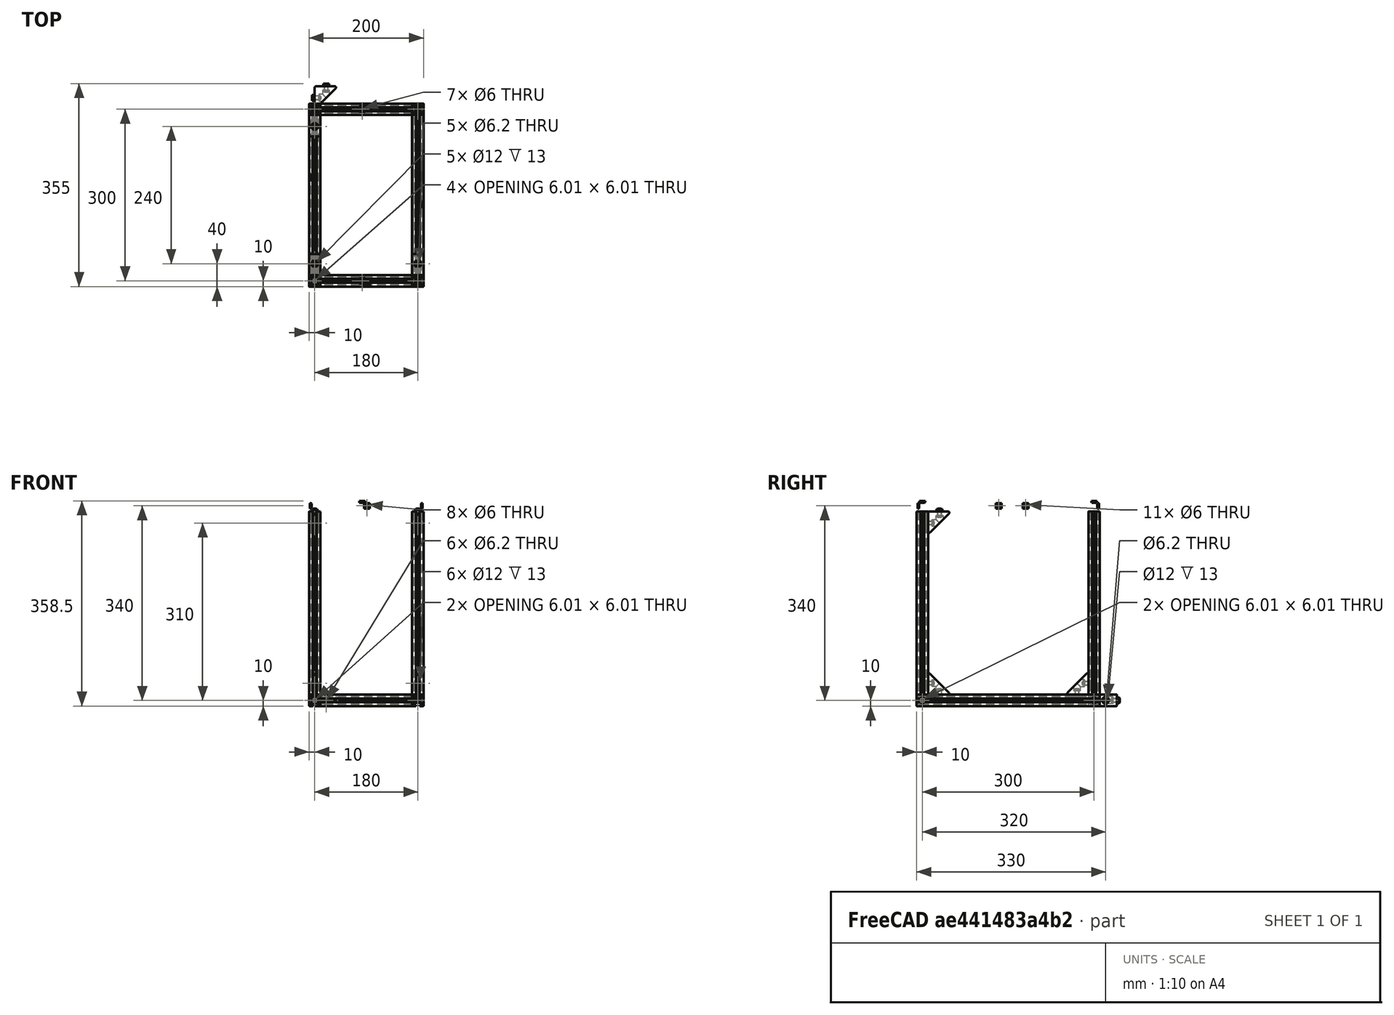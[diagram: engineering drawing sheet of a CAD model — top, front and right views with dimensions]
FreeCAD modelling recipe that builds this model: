
FCSTD DOCUMENT  (FreeCAD 0.17R9796 (Git))
Label: upperframe12
License: All rights reserved
LicenseURL: http://en.wikipedia.org/wiki/All_rights_reserved
objects: Part::Feature×55, Part::FeaturePython×16, App::Part×6, Part::Compound×5
note: 76 computed .brp shape members not serialized (recipe doc carries the construction recipe); baked Part::Feature solids carry a one-line shape summary decoded from their .brp

FEATURE [Part::Feature] Pocket003001  label="tslot32con"
  Placement = pos=(0,10,10) rot=(1,0,0;1.5708rad)
  shape: bbox 20 x 320 x 20 mm, 150 faces (baked)
FEATURE [Part::Feature] Pocket003002  label="tslot16"
  Placement = pos=(10,0,10) rot=(0,1,0;1.5708rad)
  shape: bbox 160 x 20 x 20 mm, 94 faces (baked)
FEATURE [Part::Feature] Pocket003006  label="tslot16_001"
  Placement = pos=(10,-300,10) rot=(0,1,0;1.5708rad)
  shape: bbox 160 x 20 x 20 mm, 94 faces (baked)
FEATURE [Part::Feature] Pocket003007  label="tslot32con_001"
  Placement = pos=(180,-310,10) rot=(0,0.707107,0.707107;3.14159rad)
  shape: bbox 20 x 320 x 20 mm, 150 faces (baked)
FEATURE [Part::FeaturePython] Screw  label="M6x25-Screw"  # Fasteners workbench fastener (typed FeaturePython)
  Placement = pos=(-4,0,10) rot=(0,-1,0;1.5708rad)
  diameter = 7
  invert = false
  length = 6
  matchOuter = false
  offset = 0
  thread = false
  type = 15
FEATURE [Part::FeaturePython] Screw001  label="M6x25-Screw004"  # Fasteners workbench fastener (typed FeaturePython)
  Placement = pos=(-4,-300,10) rot=(0,-1,0;1.5708rad)
  diameter = 7
  invert = false
  length = 6
  matchOuter = false
  offset = 0
  thread = false
  type = 15
FEATURE [Part::FeaturePython] Screw002  label="M6x25-Screw005"  # Fasteners workbench fastener (typed FeaturePython)
  Placement = pos=(184,0,10) rot=(0,1,0;1.5708rad)
  diameter = 7
  invert = false
  length = 6
  matchOuter = false
  offset = 0
  thread = false
  type = 15
FEATURE [Part::FeaturePython] Screw004  label="M6x25-Screw006"  # Fasteners workbench fastener (typed FeaturePython)
  Placement = pos=(184,-300,10) rot=(0,1,0;1.5708rad)
  diameter = 7
  invert = false
  length = 6
  matchOuter = false
  offset = 0
  thread = false
  type = 15
FEATURE [App::Part] Part  label="lower_frame"
  Group = -> [Pocket003001,Pocket003002,Pocket003006,Pocket003007,Screw,Screw001,Screw002,Screw004]
  License = CC BY 3.0
  LicenseURL = http://creativecommons.org/licenses/by/3.0/
  Origin = -> PartOrigin
FEATURE [Part::Feature] Pocket003008  label="tslot32con001"
  Placement = pos=(0,10,10) rot=(1,0,0;1.5708rad)
  shape: bbox 20 x 320 x 20 mm, 150 faces (baked)
FEATURE [Part::Feature] Pocket003009  label="tslot041"
  Placement = pos=(10,0,10) rot=(0,1,0;1.5708rad)
  shape: bbox 160 x 20 x 20 mm, 94 faces (baked)
FEATURE [Part::Feature] Pocket003010  label="tslot16_002"
  Placement = pos=(10,-300,10) rot=(0,1,0;1.5708rad)
  shape: bbox 160 x 20 x 20 mm, 94 faces (baked)
FEATURE [Part::Feature] Pocket003011  label="tslot32con_002"
  Placement = pos=(180,-310,10) rot=(0,0.707107,0.707107;3.14159rad)
  shape: bbox 20 x 320 x 20 mm, 150 faces (baked)
FEATURE [Part::FeaturePython] Screw005  label="M6x25-Screw012"  # Fasteners workbench fastener (typed FeaturePython)
  Placement = pos=(-4,0,10) rot=(0,-1,0;1.5708rad)
  diameter = 7
  invert = false
  length = 6
  matchOuter = false
  offset = 0
  thread = false
  type = 15
FEATURE [Part::FeaturePython] Screw006  label="M6x25-Screw015"  # Fasteners workbench fastener (typed FeaturePython)
  Placement = pos=(-4,-300,10) rot=(0,-1,0;1.5708rad)
  diameter = 7
  invert = false
  length = 6
  matchOuter = false
  offset = 0
  thread = false
  type = 15
FEATURE [Part::FeaturePython] Screw007  label="M6x25-Screw017"  # Fasteners workbench fastener (typed FeaturePython)
  Placement = pos=(184,0,10) rot=(0,1,0;1.5708rad)
  diameter = 7
  invert = false
  length = 6
  matchOuter = false
  offset = 0
  thread = false
  type = 15
FEATURE [Part::FeaturePython] Screw008  label="M6x25-Screw016"  # Fasteners workbench fastener (typed FeaturePython)
  Placement = pos=(184,-300,10) rot=(0,1,0;1.5708rad)
  diameter = 7
  invert = false
  length = 6
  matchOuter = false
  offset = 0
  thread = false
  type = 15
FEATURE [App::Part] Part001  label="upper_frame"
  Group = -> [Pocket003008,Pocket003009,Pocket003010,Pocket003011,Screw005,Screw006,Screw007,Screw008]
  License = CC BY 3.0
  LicenseURL = http://creativecommons.org/licenses/by/3.0/
  Origin = -> PartOrigin001
  Placement = pos=(0,0,340) rot=(0,0,1;0rad)
FEATURE [Part::Feature] Fillet004001  label="Fillet005"
  shape: bbox 37.5 x 37.5 x 20 mm, 26 faces (baked)
FEATURE [Part::FeaturePython] Screw009  label="M6x12-Screw"  # Fasteners workbench fastener (typed FeaturePython)
  Placement = pos=(7,20,10) rot=(0,1,0;1.5708rad)
  diameter = 4
  invert = false
  length = 1
  matchOuter = false
  offset = 0
  thread = false
  type = 20
FEATURE [Part::Feature] Body001  label="m6nutplate"
  Placement = pos=(-1.5,15,5) rot=(0,-1,0;1.5708rad)
  shape: bbox 3 x 10 x 10 mm, 9 faces (baked)
FEATURE [App::Part] Part002  label="cornerstonescrewnut"
  License = CC BY 3.0
  LicenseURL = http://creativecommons.org/licenses/by/3.0/
  Origin = -> PartOrigin002
  Placement = pos=(10,-50,20) rot=(0,-1,0;1.5708rad)
FEATURE [Part::FeaturePython] Screw010  label="M6x12-Screw001"  # Fasteners workbench fastener (typed FeaturePython)
  Placement = pos=(20,33,10) rot=(1,0,0;1.5708rad)
  diameter = 4
  invert = false
  length = 1
  matchOuter = false
  offset = 0
  thread = false
  type = 20
FEATURE [Part::Feature] Body002  label="m6nutplate001"
  Placement = pos=(15,41.5,5) rot=(0.57735,0.57735,0.57735;4.18879rad)
  shape: bbox 10 x 3 x 10 mm, 9 faces (baked)
FEATURE [Part::Feature] Fillet004002  label="Fillet006"
  shape: bbox 37.5 x 37.5 x 20 mm, 26 faces (baked)
FEATURE [Part::FeaturePython] Screw011  label="M6x12-Screw002"  # Fasteners workbench fastener (typed FeaturePython)
  Placement = pos=(7,20,10) rot=(0,1,0;1.5708rad)
  diameter = 4
  invert = false
  length = 1
  matchOuter = false
  offset = 0
  thread = false
  type = 20
FEATURE [Part::Feature] Body003  label="m6nutplate002"
  Placement = pos=(-1.5,15,5) rot=(0,-1,0;1.5708rad)
  shape: bbox 3 x 10 x 10 mm, 9 faces (baked)
FEATURE [Part::FeaturePython] Screw012  label="M6x12-Screw003"  # Fasteners workbench fastener (typed FeaturePython)
  Placement = pos=(20,33,10) rot=(1,0,0;1.5708rad)
  diameter = 4
  invert = false
  length = 1
  matchOuter = false
  offset = 0
  thread = false
  type = 20
FEATURE [Part::Feature] Body004  label="m6nutplate003"
  Placement = pos=(15,41.5,5) rot=(0.57735,0.57735,0.57735;4.18879rad)
  shape: bbox 10 x 3 x 10 mm, 9 faces (baked)
FEATURE [App::Part] Part003  label="cornerstonescrewnut001"
  Group = -> [Body003,Screw011,Fillet004002,Screw012,Body004,PartOrigin002,Body001,Screw009,Fillet004001,Screw010,Body002,Part002]
  License = CC BY 3.0
  LicenseURL = http://creativecommons.org/licenses/by/3.0/
  Origin = -> PartOrigin003
  Placement = pos=(190,-50,20) rot=(0,-1,0;1.5708rad)
FEATURE [Part::Feature] Fillet004003  label="Fillet007"
  shape: bbox 37.5 x 37.5 x 20 mm, 26 faces (baked)
FEATURE [Part::FeaturePython] Screw013  label="M6x12-Screw004"  # Fasteners workbench fastener (typed FeaturePython)
  Placement = pos=(7,20,10) rot=(0,1,0;1.5708rad)
  diameter = 4
  invert = false
  length = 1
  matchOuter = false
  offset = 0
  thread = false
  type = 20
FEATURE [Part::Feature] Body005  label="m6nutplate004"
  Placement = pos=(-1.5,15,5) rot=(0,-1,0;1.5708rad)
  shape: bbox 3 x 10 x 10 mm, 9 faces (baked)
FEATURE [Part::FeaturePython] Screw014  label="M6x12-Screw005"  # Fasteners workbench fastener (typed FeaturePython)
  Placement = pos=(20,33,10) rot=(1,0,0;1.5708rad)
  diameter = 4
  invert = false
  length = 1
  matchOuter = false
  offset = 0
  thread = false
  type = 20
FEATURE [Part::Feature] Body006  label="m6nutplate005"
  Placement = pos=(15,41.5,5) rot=(0.57735,0.57735,0.57735;4.18879rad)
  shape: bbox 10 x 3 x 10 mm, 9 faces (baked)
FEATURE [App::Part] Part004  label="cornerstonescrewnut002"
  Group = -> [Body005,Screw013,Fillet004003,Screw014,Body006]
  License = CC BY 3.0
  LicenseURL = http://creativecommons.org/licenses/by/3.0/
  Origin = -> PartOrigin004
  Placement = pos=(-10,-50,340) rot=(0,1,0;1.5708rad)
FEATURE [Part::Feature] Fillet004004  label="Fillet008"
  shape: bbox 37.5 x 37.5 x 20 mm, 26 faces (baked)
FEATURE [Part::FeaturePython] Screw015  label="M6x12-Screw006"  # Fasteners workbench fastener (typed FeaturePython)
  Placement = pos=(7,20,10) rot=(0,1,0;1.5708rad)
  diameter = 4
  invert = false
  length = 1
  matchOuter = false
  offset = 0
  thread = false
  type = 20
FEATURE [Part::Feature] Body007  label="m6nutplate006"
  Placement = pos=(-1.5,15,5) rot=(0,-1,0;1.5708rad)
  shape: bbox 3 x 10 x 10 mm, 9 faces (baked)
FEATURE [Part::FeaturePython] Screw016  label="M6x12-Screw007"  # Fasteners workbench fastener (typed FeaturePython)
  Placement = pos=(20,33,10) rot=(1,0,0;1.5708rad)
  diameter = 4
  invert = false
  length = 1
  matchOuter = false
  offset = 0
  thread = false
  type = 20
FEATURE [Part::Feature] Body008  label="m6nutplate007"
  Placement = pos=(15,41.5,5) rot=(0.57735,0.57735,0.57735;4.18879rad)
  shape: bbox 10 x 3 x 10 mm, 9 faces (baked)
FEATURE [App::Part] Part005  label="cornerstonescrewnut003"
  Group = -> [Body007,Screw015,Fillet004004,Screw016,Body008]
  License = CC BY 3.0
  LicenseURL = http://creativecommons.org/licenses/by/3.0/
  Origin = -> PartOrigin005
  Placement = pos=(170,-50,340) rot=(0,1,0;1.5708rad)
FEATURE [Part::Feature] Body009001  label="m6nutplate010"
  Placement = pos=(-1.5,15,5) rot=(0,-1,0;1.5708rad)
  shape: bbox 3 x 10 x 10 mm, 9 faces (baked)
FEATURE [Part::Feature] Body010001  label="m6nutplate011"
  Placement = pos=(15,41.5,5) rot=(0.57735,0.57735,0.57735;4.18879rad)
  shape: bbox 10 x 3 x 10 mm, 9 faces (baked)
FEATURE [Part::Feature] Screw018001  label="M6x12-Screw010"
  Placement = pos=(20,33,10) rot=(1,0,0;1.5708rad)
  shape: bbox 10.5 x 15.3 x 10.5 mm, 15 faces (baked)
FEATURE [Part::Feature] Screw017001  label="M6x12-Screw011"
  Placement = pos=(7,20,10) rot=(0,1,0;1.5708rad)
  shape: bbox 15.3 x 10.5 x 10.5 mm, 15 faces (baked)
FEATURE [Part::Feature] Fillet004005001  label="Fillet010"
  shape: bbox 37.5 x 37.5 x 20 mm, 26 faces (baked)
FEATURE [Part::Compound] Compound
  Links = -> [Body009001,Fillet004005001,Screw017001,Body010001,Screw018001]
  Placement = pos=(10,-250,340) rot=(0.707107,0,-0.707107;3.14159rad)
FEATURE [Part::Feature] Body010002  label="m6nutplate012"
  Placement = pos=(-1.5,15,5) rot=(0,-1,0;1.5708rad)
  shape: bbox 3 x 10 x 10 mm, 9 faces (baked)
FEATURE [Part::Feature] Body010003  label="m6nutplate013"
  Placement = pos=(15,41.5,5) rot=(0.57735,0.57735,0.57735;4.18879rad)
  shape: bbox 10 x 3 x 10 mm, 9 faces (baked)
FEATURE [Part::Feature] Screw018002  label="M6x12-Screw012"
  Placement = pos=(20,33,10) rot=(1,0,0;1.5708rad)
  shape: bbox 10.5 x 15.3 x 10.5 mm, 15 faces (baked)
FEATURE [Part::Feature] Screw018003  label="M6x12-Screw013"
  Placement = pos=(7,20,10) rot=(0,1,0;1.5708rad)
  shape: bbox 15.3 x 10.5 x 10.5 mm, 15 faces (baked)
FEATURE [Part::Feature] Fillet004005002  label="Fillet011"
  shape: bbox 37.5 x 37.5 x 20 mm, 26 faces (baked)
FEATURE [Part::Compound] Compound001
  Links = -> [Body010002,Fillet004005002,Screw018003,Body010003,Screw018002]
  Placement = pos=(190,-250,340) rot=(0.707107,0,-0.707107;3.14159rad)
FEATURE [Part::Feature] Body010004  label="m6nutplate014"
  Placement = pos=(-1.5,15,5) rot=(0,-1,0;1.5708rad)
  shape: bbox 3 x 10 x 10 mm, 9 faces (baked)
FEATURE [Part::Feature] Body010005  label="m6nutplate015"
  Placement = pos=(15,41.5,5) rot=(0.57735,0.57735,0.57735;4.18879rad)
  shape: bbox 10 x 3 x 10 mm, 9 faces (baked)
FEATURE [Part::Feature] Screw018004  label="M6x12-Screw014"
  Placement = pos=(20,33,10) rot=(1,0,0;1.5708rad)
  shape: bbox 10.5 x 15.3 x 10.5 mm, 15 faces (baked)
FEATURE [Part::Feature] Screw018005  label="M6x12-Screw015"
  Placement = pos=(7,20,10) rot=(0,1,0;1.5708rad)
  shape: bbox 15.3 x 10.5 x 10.5 mm, 15 faces (baked)
FEATURE [Part::Feature] Fillet004005003  label="Fillet012"
  shape: bbox 37.5 x 37.5 x 20 mm, 26 faces (baked)
FEATURE [Part::Compound] Compound002
  Links = -> [Body010004,Fillet004005003,Screw018005,Body010005,Screw018004]
  Placement = pos=(10,-290,60) rot=(0.57735,0.57735,-0.57735;4.18879rad)
FEATURE [Part::Feature] Body010006  label="m6nutplate016"
  Placement = pos=(-1.5,15,5) rot=(0,-1,0;1.5708rad)
  shape: bbox 3 x 10 x 10 mm, 9 faces (baked)
FEATURE [Part::Feature] Body010007  label="m6nutplate017"
  Placement = pos=(15,41.5,5) rot=(0.57735,0.57735,0.57735;4.18879rad)
  shape: bbox 10 x 3 x 10 mm, 9 faces (baked)
FEATURE [Part::Feature] Screw018006  label="M6x12-Screw016"
  Placement = pos=(20,33,10) rot=(1,0,0;1.5708rad)
  shape: bbox 10.5 x 15.3 x 10.5 mm, 15 faces (baked)
FEATURE [Part::Feature] Screw018007  label="M6x12-Screw017"
  Placement = pos=(7,20,10) rot=(0,1,0;1.5708rad)
  shape: bbox 15.3 x 10.5 x 10.5 mm, 15 faces (baked)
FEATURE [Part::Feature] Fillet004005004  label="Fillet013"
  shape: bbox 37.5 x 37.5 x 20 mm, 26 faces (baked)
FEATURE [Part::Compound] Compound003
  Links = -> [Body010006,Fillet004005004,Screw018007,Body010007,Screw018006]
  Placement = pos=(190,-290,60) rot=(0.57735,0.57735,-0.57735;4.18879rad)
FEATURE [Part::Feature] Pocket001001  label="tslot32"
  Placement = pos=(0,0,20) rot=(0,0,1;0rad)
  shape: bbox 20 x 20 x 320 mm, 94 faces (baked)
FEATURE [Part::Feature] Body010008  label="m6nutplate018"
  Placement = pos=(-1.5,15,5) rot=(0,-1,0;1.5708rad)
  shape: bbox 3 x 10 x 10 mm, 9 faces (baked)
FEATURE [Part::Feature] Body010009  label="m6nutplate019"
  Placement = pos=(15,41.5,5) rot=(0.57735,0.57735,0.57735;4.18879rad)
  shape: bbox 10 x 3 x 10 mm, 9 faces (baked)
FEATURE [Part::Feature] Screw018008  label="M6x12-Screw018"
  Placement = pos=(20,33,10) rot=(1,0,0;1.5708rad)
  shape: bbox 10.5 x 15.3 x 10.5 mm, 15 faces (baked)
FEATURE [Part::Feature] Screw018009  label="M6x12-Screw019"
  Placement = pos=(7,20,10) rot=(0,1,0;1.5708rad)
  shape: bbox 15.3 x 10.5 x 10.5 mm, 15 faces (baked)
FEATURE [Part::Feature] Fillet004005005  label="Fillet014"
  shape: bbox 37.5 x 37.5 x 20 mm, 26 faces (baked)
FEATURE [Part::Compound] Compound004
  Links = -> [Body010008,Fillet004005005,Screw018009,Body010009,Screw018008]
  Placement = pos=(-10,-10,60) rot=(0.57735,-0.57735,0.57735;4.18879rad)
FEATURE [Part::Feature] Pocket003012  label="tslot32_001"
  Placement = pos=(0,-300,20) rot=(0,0,1;0rad)
  shape: bbox 20 x 20 x 320 mm, 94 faces (baked)
FEATURE [Part::Feature] Pocket003013  label="tslot32_002"
  Placement = pos=(180,0,20) rot=(0,0,1;0rad)
  shape: bbox 20 x 20 x 320 mm, 94 faces (baked)
FEATURE [Part::Feature] Pocket003014  label="tslot32_003"
  Placement = pos=(180,-300,20) rot=(0,0,1;0rad)
  shape: bbox 20 x 20 x 320 mm, 94 faces (baked)
FEATURE [Part::Feature] Chamfer001001  label="m6nutplate020"
  Placement = pos=(88,-295,358.5) rot=(0.707107,-0.707107,0;3.14159rad)
  shape: bbox 10 x 10 x 3 mm, 9 faces (baked)
FEATURE [Part::Feature] Chamfer001002  label="m6nutplate021"
  Placement = pos=(96,-308.5,355) rot=(0.57735,-0.57735,-0.57735;4.18879rad)
  shape: bbox 10 x 3 x 10 mm, 9 faces (baked)
FEATURE [Part::Feature] Chamfer001003  label="m6nutplate022"
  Placement = pos=(-8.5,-124.5,355) rot=(0,1,0;1.5708rad)
  shape: bbox 3 x 10 x 10 mm, 9 faces (baked)
FEATURE [Part::Feature] Chamfer001004  label="m6nutplate023"
  Placement = pos=(88,5,358.5) rot=(0.707107,-0.707107,0;3.14159rad)
  shape: bbox 10 x 10 x 3 mm, 9 faces (baked)
FEATURE [Part::Feature] Chamfer001005  label="m6nutplate024"
  Placement = pos=(96,8.5,345) rot=(0.57735,-0.57735,0.57735;2.0944rad)
  shape: bbox 10 x 3 x 10 mm, 9 faces (baked)
FEATURE [Part::Feature] Chamfer001006  label="m6nutplate025"
  Placement = pos=(188.5,-171.5,345) rot=(0,1,0;4.71239rad)
  shape: bbox 3 x 10 x 10 mm, 9 faces (baked)
